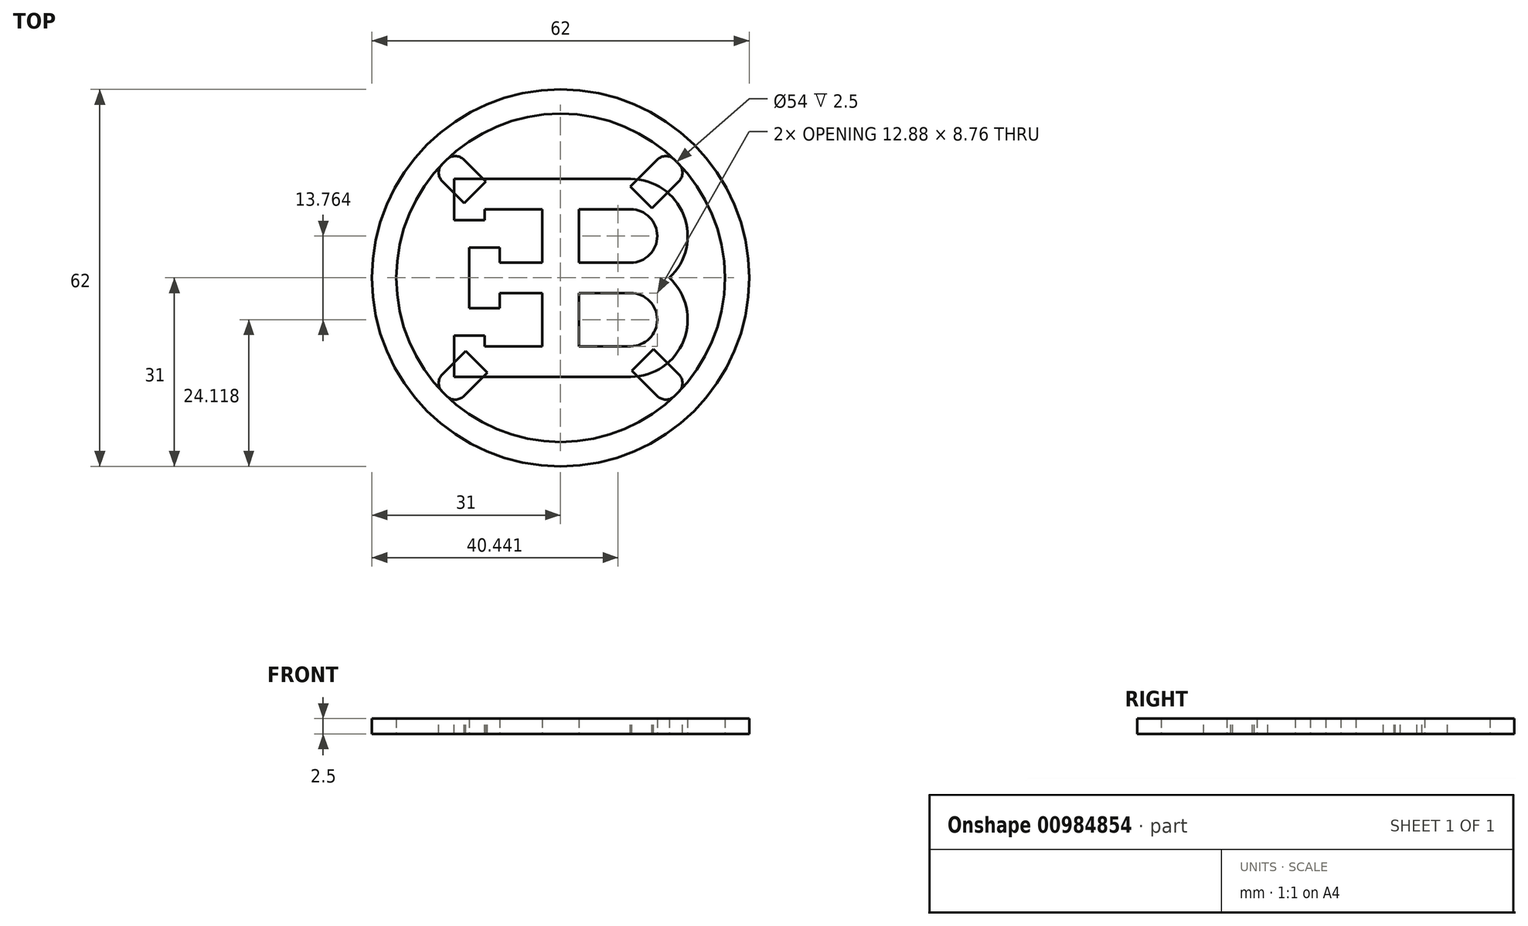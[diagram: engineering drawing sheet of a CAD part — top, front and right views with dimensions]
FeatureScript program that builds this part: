
annotation { "Feature Type Name" : "Feature", "Feature Type Description" : "" }
export const myFeature = defineFeature(function(context is Context, id is Id, definition is map)
    precondition{}
    {
        {
            var Q0;
            Q0=qCreatedBy(makeId("Front.planeOp"),FACE);
            var sketch = newSketch(context, id + "F0", { "sketchPlane" : qUnion([Q0])});
            skLineSegment(sketch, "E0.bottom", {"start": v(27, 0) * mm, "end": v(31, 0) * mm});
            skLineSegment(sketch, "E0.top", {"start": v(27, 2.5) * mm, "end": v(31, 2.5) * mm});
            skLineSegment(sketch, "E0.right", {"start": v(31, 0) * mm, "end": v(31, 2.5) * mm});
            skLineSegment(sketch, "E1", {"start": v(27, 2.5) * mm, "end": v(27, 0) * mm});
            skLineSegment(sketch, "E2", {"start": v(0, 0) * mm, "end": v(0, 16.47) * mm, "construction": true});
            skSolve(sketch);
        }
        {
            var Q0;
            Q0=qSketchRegion(id+"F0",true);
            var Q1;
            Q1=sQuery(id+"F0.wireOp",EDGE,"E2");
            revolve(context, id + "F1", {"surfaceOperationType" : NewSurfaceOperationType.NEW, "entities" : qUnion([Q0]), "axis" : qUnion([Q1]), "revolveType" : RevolveType.FULL});
        }
        {
            var Q0;
            Q0=qCreatedBy(makeId("Top.planeOp"),FACE);
            var sketch = newSketch(context, id + "F2", { "sketchPlane" : qUnion([Q0])});
            skLineSegment(sketch, "E3", {"start": v(0, 0) * mm, "end": v(-19.1, 19.1) * mm, "construction": true});
            skLineSegment(sketch, "E4", {"start": v(0, 0) * mm, "end": v(-19.1, -19.1) * mm, "construction": true});
            skLineSegment(sketch, "E5", {"start": v(0, 0) * mm, "end": v(-27, 0) * mm, "construction": true});
            skLineSegment(sketch, "E6", {"start": v(0, 0) * mm, "end": v(0, 27) * mm, "construction": true});
            skLineSegment(sketch, "E7", {"start": v(0, 0) * mm, "end": v(0, -27) * mm, "construction": true});
            skCircle(sketch, "E8", {"center": v(0, 0) * mm, "radius": 23 * mm, "construction": true});
            skLineSegment(sketch, "E9", {"start": v(-16.26, 16.26) * mm, "end": v(11.5, 16.26) * mm});
            skLineSegment(sketch, "E10", {"start": v(11.5, -16.26) * mm, "end": v(-16.26, -16.26) * mm});
            skLineSegment(sketch, "E11", {"start": v(-16.26, -16.26) * mm, "end": v(-16.26, -11.26) * mm});
            skLineSegment(sketch, "E12", {"start": v(-16.26, 11.26) * mm, "end": v(-3, 11.26) * mm});
            skLineSegment(sketch, "E13", {"start": v(-3, 11.26) * mm, "end": v(-3, 2.5) * mm});
            skLineSegment(sketch, "E14", {"start": v(-3, -11.26) * mm, "end": v(-16.26, -11.26) * mm});
            skLineSegment(sketch, "E15.trimOffspring", {"start": v(-16.26, 11.26) * mm, "end": v(-16.26, 16.26) * mm});
            skPoint(sketch, "E16.first.point", {"position": v(11.5, 16.26) * mm});
            skPoint(sketch, "E16.third.point", {"position": v(19.26, 12.58) * mm});
            skLineSegment(sketch, "E17", {"start": v(-3, 2.5) * mm, "end": v(-10, 2.5) * mm});
            skLineSegment(sketch, "E18", {"start": v(-10, -2.5) * mm, "end": v(-3, -2.5) * mm});
            skLineSegment(sketch, "E19.trimOffspring", {"start": v(-3, -2.5) * mm, "end": v(-3, -11.26) * mm});
            skLineSegment(sketch, "E20", {"start": v(-3, 2.5) * mm, "end": v(22.86, 2.5) * mm, "construction": true});
            skLineSegment(sketch, "E21", {"start": v(-3, -2.5) * mm, "end": v(22.86, -2.5) * mm, "construction": true});
            skLineSegment(sketch, "E22", {"start": v(3, 2.5) * mm, "end": v(3, 11.26) * mm});
            skLineSegment(sketch, "E23", {"start": v(3, 11.26) * mm, "end": v(11.5, 11.26) * mm});
            skLineSegment(sketch, "E24", {"start": v(3, 2.5) * mm, "end": v(11.5, 2.5) * mm});
            skArc(sketch, "E25", {"start": v(11.5, 11.26) * mm, "mid": v(15.88, 6.88) * mm, "end": v(11.5, 2.5) * mm});
            skArc(sketch, "E26.MirrorCS", {"start": v(11.5, -11.26) * mm, "mid": v(15.88, -6.88) * mm, "end": v(11.5, -2.5) * mm});
            skLineSegment(sketch, "E27.MirrorCS", {"start": v(3, -2.5) * mm, "end": v(3, -11.26) * mm});
            skLineSegment(sketch, "E28.MirrorCS", {"start": v(3, -11.26) * mm, "end": v(11.5, -11.26) * mm});
            skArc(sketch, "E29.trimOffspring", {"start": v(17.88, 0) * mm, "mid": v(20.23, -10.3) * mm, "end": v(11.5, -16.26) * mm});
            skArc(sketch, "E30.trimOffspring", {"start": v(17.88, 0) * mm, "mid": v(20.23, 10.3) * mm, "end": v(11.5, 16.26) * mm});
            skLineSegment(sketch, "E31", {"start": v(11.5, -2.5) * mm, "end": v(3, -2.5) * mm});
            skLineSegment(sketch, "E32.MirrorCS", {"start": v(0, 0) * mm, "end": v(19.1, 19.1) * mm, "construction": true});
            skLineSegment(sketch, "E33.MirrorCS", {"start": v(0, 0) * mm, "end": v(19.1, -19.1) * mm, "construction": true});
            skLineSegment(sketch, "E34.bottom", {"start": v(-15, -5) * mm, "end": v(-10, -5) * mm});
            skLineSegment(sketch, "E34.top", {"start": v(-15, 5) * mm, "end": v(-10, 5) * mm});
            skLineSegment(sketch, "E34.left", {"start": v(-15, -5) * mm, "end": v(-15, 5) * mm});
            skLineSegment(sketch, "E34.right", {"start": v(-10, -5) * mm, "end": v(-10, -2.5) * mm});
            skLineSegment(sketch, "E35.trimOffspring", {"start": v(-10, 2.5) * mm, "end": v(-10, 5) * mm});
            skSolve(sketch);
        }
        {
            var Q0;
            Q0=makeQuery(id+"F2.imprint","IMPRINT",FACE,{"disambiguationData":[TD([[makeQuery(id+"F2.imprint","IMPRINT",EDGE,{"derivedFrom":sQuery(id+"F2.wireOp",EDGE,"E9")}),-1.0]])]});
            var Q1;
            Q1=makeQuery(id+"F1.opRevolve","SWEPT_FACE",FACE,{"disambiguationData":[OSD([sQuery(id+"F0.wireOp",EDGE,"E0.top")])]});
            extrude(context, id + "F3", {"entities" : qUnion([Q0]), "endBound" : BoundingType.UP_TO_SURFACE, "depth" : 25 * mm, "endBoundEntityFace" : qUnion([Q1]), "offsetDistance" : 25 * mm});
        }
        {
            var Q0;
            Q0=makeQuery(id+"F3.opExtrude","CAP_FACE",FACE,{"disambiguationData":[OSD([sQuery(id+"F2.wireOp",EDGE,"E9"),sQuery(id+"F2.wireOp",EDGE,"E10"),sQuery(id+"F2.wireOp",EDGE,"E11"),sQuery(id+"F2.wireOp",EDGE,"E12"),sQuery(id+"F2.wireOp",EDGE,"E13"),sQuery(id+"F2.wireOp",EDGE,"E14"),sQuery(id+"F2.wireOp",EDGE,"E15.trimOffspring"),sQuery(id+"F2.wireOp",EDGE,"E17"),sQuery(id+"F2.wireOp",EDGE,"E18"),sQuery(id+"F2.wireOp",EDGE,"E19.trimOffspring"),sQuery(id+"F2.wireOp",EDGE,"E22"),sQuery(id+"F2.wireOp",EDGE,"E23"),sQuery(id+"F2.wireOp",EDGE,"E24"),sQuery(id+"F2.wireOp",EDGE,"E25"),sQuery(id+"F2.wireOp",EDGE,"E26.MirrorCS"),sQuery(id+"F2.wireOp",EDGE,"E27.MirrorCS"),sQuery(id+"F2.wireOp",EDGE,"E28.MirrorCS"),sQuery(id+"F2.wireOp",EDGE,"E29.trimOffspring"),sQuery(id+"F2.wireOp",EDGE,"E30.trimOffspring"),sQuery(id+"F2.wireOp",EDGE,"E31"),sQuery(id+"F2.wireOp",EDGE,"E34.bottom"),sQuery(id+"F2.wireOp",EDGE,"E34.top"),sQuery(id+"F2.wireOp",EDGE,"E34.left"),sQuery(id+"F2.wireOp",EDGE,"E34.right"),sQuery(id+"F2.wireOp",EDGE,"E35.trimOffspring")])],"isStart":false});
            var sketch = newSketch(context, id + "F4", { "sketchPlane" : qUnion([Q0])});
            skLineSegment(sketch, "E36", {"start": v(-12.5, 5) * mm, "end": v(-12.5, 16.26) * mm, "construction": true});
            skLineSegment(sketch, "E37", {"start": v(-12.5, -5) * mm, "end": v(-12.5, -16.26) * mm, "construction": true});
            skLineSegment(sketch, "E38.bottom", {"start": v(-12.5, 9.51) * mm, "end": v(-17.5, 9.51) * mm});
            skLineSegment(sketch, "E38.top", {"start": v(-12.5, 16.26) * mm, "end": v(-17.5, 16.26) * mm});
            skLineSegment(sketch, "E38.left", {"start": v(-12.5, 9.51) * mm, "end": v(-12.5, 16.26) * mm});
            skLineSegment(sketch, "E38.right", {"start": v(-17.5, 9.51) * mm, "end": v(-17.5, 16.26) * mm});
            skLineSegment(sketch, "E39.MirrorCS", {"start": v(-12.5, -9.51) * mm, "end": v(-17.5, -9.51) * mm});
            skLineSegment(sketch, "E40.MirrorCS", {"start": v(-12.5, -9.51) * mm, "end": v(-12.5, -16.26) * mm});
            skLineSegment(sketch, "E41.MirrorCS", {"start": v(-17.5, -9.51) * mm, "end": v(-17.5, -16.26) * mm});
            skLineSegment(sketch, "E42.MirrorCS", {"start": v(-12.5, -16.26) * mm, "end": v(-17.5, -16.26) * mm});
            skSolve(sketch);
        }
        {
            var Q0;
            {var subQ1=sQuery(id+"F4.wireOp",EDGE,"E38.bottom");Q0=makeQuery(id+"F4.imprint","IMPRINT",FACE,{"disambiguationData":[TD([[makeQuery(id+"F4.imprint","IMPRINT",EDGE,{"derivedFrom":subQ1}),-1.0]])]});}
            var Q1;
            {var subQ2=sQuery(id+"F4.wireOp",EDGE,"E39.MirrorCS");Q1=makeQuery(id+"F4.imprint","IMPRINT",FACE,{"disambiguationData":[TD([[makeQuery(id+"F4.imprint","IMPRINT",EDGE,{"derivedFrom":subQ2}),1.0]])]});}
            var Q2;
            Q2=makeQuery(id+"F3.opExtrude","CAP_FACE",FACE,{"disambiguationData":[OSD([sQuery(id+"F2.wireOp",EDGE,"E9"),sQuery(id+"F2.wireOp",EDGE,"E10"),sQuery(id+"F2.wireOp",EDGE,"E11"),sQuery(id+"F2.wireOp",EDGE,"E12"),sQuery(id+"F2.wireOp",EDGE,"E13"),sQuery(id+"F2.wireOp",EDGE,"E14"),sQuery(id+"F2.wireOp",EDGE,"E15.trimOffspring"),sQuery(id+"F2.wireOp",EDGE,"E17"),sQuery(id+"F2.wireOp",EDGE,"E18"),sQuery(id+"F2.wireOp",EDGE,"E19.trimOffspring"),sQuery(id+"F2.wireOp",EDGE,"E22"),sQuery(id+"F2.wireOp",EDGE,"E23"),sQuery(id+"F2.wireOp",EDGE,"E24"),sQuery(id+"F2.wireOp",EDGE,"E25"),sQuery(id+"F2.wireOp",EDGE,"E26.MirrorCS"),sQuery(id+"F2.wireOp",EDGE,"E27.MirrorCS"),sQuery(id+"F2.wireOp",EDGE,"E28.MirrorCS"),sQuery(id+"F2.wireOp",EDGE,"E29.trimOffspring"),sQuery(id+"F2.wireOp",EDGE,"E30.trimOffspring"),sQuery(id+"F2.wireOp",EDGE,"E31"),sQuery(id+"F2.wireOp",EDGE,"E34.bottom"),sQuery(id+"F2.wireOp",EDGE,"E34.top"),sQuery(id+"F2.wireOp",EDGE,"E34.left"),sQuery(id+"F2.wireOp",EDGE,"E34.right"),sQuery(id+"F2.wireOp",EDGE,"E35.trimOffspring")])],"isStart":true});
            extrude(context, id + "F5", {"entities" : qUnion([Q0, Q1]), "operationType" : NewBodyOperationType.ADD, "endBound" : BoundingType.UP_TO_SURFACE, "oppositeDirection" : true, "depth" : 25 * mm, "endBoundEntityFace" : qUnion([Q2]), "offsetDistance" : 25 * mm});
        }
        {
            var Q0;
            Q0=makeQuery(id+"F1.opRevolve","SWEPT_FACE",FACE,{"disambiguationData":[OSD([sQuery(id+"F0.wireOp",EDGE,"E0.top")])]});
            var sketch = newSketch(context, id + "F6", { "sketchPlane" : qUnion([Q0])});
            skLineSegment(sketch, "E43", {"start": v(0, 0) * mm, "end": v(-19.1, 19.1) * mm, "construction": true});
            skLineSegment(sketch, "E44", {"start": v(0, 0) * mm, "end": v(-19.1, -19.1) * mm, "construction": true});
            skLineSegment(sketch, "E45", {"start": v(0, 0) * mm, "end": v(19.1, 19.1) * mm, "construction": true});
            skLineSegment(sketch, "E46", {"start": v(0, 0) * mm, "end": v(19.1, -19.1) * mm, "construction": true});
            skLineSegment(sketch, "E47", {"start": v(-17.24, 20.78) * mm, "end": v(-12.28, 15.82) * mm});
            skLineSegment(sketch, "E48", {"start": v(-12.28, 15.82) * mm, "end": v(-15.82, 12.28) * mm});
            skLineSegment(sketch, "E49", {"start": v(-15.82, 12.28) * mm, "end": v(-20.78, 17.24) * mm});
            skLineSegment(sketch, "E50", {"start": v(17.24, -20.78) * mm, "end": v(11.74, -15.28) * mm});
            skLineSegment(sketch, "E51", {"start": v(11.74, -15.28) * mm, "end": v(15.28, -11.74) * mm});
            skLineSegment(sketch, "E52", {"start": v(15.28, -11.74) * mm, "end": v(20.78, -17.24) * mm});
            skLineSegment(sketch, "E53", {"start": v(-20.78, -17.24) * mm, "end": v(-15.6, -12.07) * mm});
            skLineSegment(sketch, "E54", {"start": v(-15.6, -12.07) * mm, "end": v(-12.06, -15.6) * mm});
            skLineSegment(sketch, "E55", {"start": v(-12.06, -15.6) * mm, "end": v(-17.24, -20.78) * mm});
            skLineSegment(sketch, "E56", {"start": v(17.24, 20.78) * mm, "end": v(11.47, 15) * mm});
            skLineSegment(sketch, "E57", {"start": v(11.47, 15) * mm, "end": v(15, 11.47) * mm});
            skLineSegment(sketch, "E58", {"start": v(15, 11.47) * mm, "end": v(20.78, 17.24) * mm});
            skSolve(sketch);
        }
        {
            var Q0;
            {var subQ0=sQuery(id+"F6.wireOp",EDGE,"E47");Q0=makeQuery(id+"F6.imprint","IMPRINT",FACE,{"disambiguationData":[TD([[makeQuery(id+"F6.imprint","IMPRINT",EDGE,{"derivedFrom":subQ0}),-1.0]])]});}
            var Q1;
            {var subQ0=sQuery(id+"F6.wireOp",EDGE,"E56");Q1=makeQuery(id+"F6.imprint","IMPRINT",FACE,{"disambiguationData":[TD([[makeQuery(id+"F6.imprint","IMPRINT",EDGE,{"derivedFrom":subQ0}),1.0]])]});}
            var Q2;
            {var subQ0=sQuery(id+"F6.wireOp",EDGE,"E50");Q2=makeQuery(id+"F6.imprint","IMPRINT",FACE,{"disambiguationData":[TD([[makeQuery(id+"F6.imprint","IMPRINT",EDGE,{"derivedFrom":subQ0}),-1.0]])]});}
            var Q3;
            {var subQ0=sQuery(id+"F6.wireOp",EDGE,"E53");Q3=makeQuery(id+"F6.imprint","IMPRINT",FACE,{"disambiguationData":[TD([[makeQuery(id+"F6.imprint","IMPRINT",EDGE,{"derivedFrom":subQ0}),-1.0]])]});}
            var Q4;
            Q4=makeQuery(id+"F1.opRevolve","SWEPT_FACE",FACE,{"disambiguationData":[OSD([sQuery(id+"F0.wireOp",EDGE,"E0.bottom")])]});
            extrude(context, id + "F7", {"entities" : qUnion([Q0, Q1, Q2, Q3]), "endBound" : BoundingType.UP_TO_SURFACE, "oppositeDirection" : true, "depth" : 25 * mm, "endBoundEntityFace" : qUnion([Q4]), "offsetDistance" : 25 * mm});
        }
        {
            var Q0;
            Q0=makeQuery(id+"F7.opExtrude","SWEPT_EDGE",EDGE,{"disambiguationData":[OSD([sQuery(id+"F0.wireOp",EDGE,"E0.top"),sQuery(id+"F0.wireOp",EDGE,"E1"),sQuery(id+"F6.wireOp",EDGE,"E47")])]});
            var Q1;
            Q1=makeQuery(id+"F7.opExtrude","SWEPT_EDGE",EDGE,{"disambiguationData":[OSD([sQuery(id+"F0.wireOp",EDGE,"E0.top"),sQuery(id+"F0.wireOp",EDGE,"E1"),sQuery(id+"F6.wireOp",EDGE,"E56")])]});
            fillet(context, id + "F8", {"entities" : qUnion([Q0, Q1]), "radius" : 2 * mm, "tangentPropagation" : true, "allowEdgeOverflow" : false});
        }
        {
            var Q0;
            Q0=makeQuery(id+"F7.opExtrude","SWEPT_EDGE",EDGE,{"disambiguationData":[OSD([sQuery(id+"F0.wireOp",EDGE,"E0.top"),sQuery(id+"F0.wireOp",EDGE,"E1"),sQuery(id+"F6.wireOp",EDGE,"E49")])]});
            var Q1;
            Q1=makeQuery(id+"F7.opExtrude","SWEPT_EDGE",EDGE,{"disambiguationData":[OSD([sQuery(id+"F0.wireOp",EDGE,"E0.top"),sQuery(id+"F0.wireOp",EDGE,"E1"),sQuery(id+"F6.wireOp",EDGE,"E53")])]});
            fillet(context, id + "F9", {"entities" : qUnion([Q0, Q1]), "radius" : 2 * mm, "tangentPropagation" : true, "allowEdgeOverflow" : false});
        }
        {
            var Q0;
            Q0=makeQuery(id+"F7.opExtrude","SWEPT_EDGE",EDGE,{"disambiguationData":[OSD([sQuery(id+"F0.wireOp",EDGE,"E0.top"),sQuery(id+"F0.wireOp",EDGE,"E1"),sQuery(id+"F6.wireOp",EDGE,"E55")])]});
            var Q1;
            Q1=makeQuery(id+"F7.opExtrude","SWEPT_EDGE",EDGE,{"disambiguationData":[OSD([sQuery(id+"F0.wireOp",EDGE,"E0.top"),sQuery(id+"F0.wireOp",EDGE,"E1"),sQuery(id+"F6.wireOp",EDGE,"E50")])]});
            fillet(context, id + "F10", {"entities" : qUnion([Q0, Q1]), "radius" : 2 * mm, "tangentPropagation" : true, "allowEdgeOverflow" : false});
        }
        {
            var Q0;
            Q0=makeQuery(id+"F7.opExtrude","SWEPT_EDGE",EDGE,{"disambiguationData":[OSD([sQuery(id+"F0.wireOp",EDGE,"E0.top"),sQuery(id+"F0.wireOp",EDGE,"E1"),sQuery(id+"F6.wireOp",EDGE,"E58")])]});
            var Q1;
            Q1=makeQuery(id+"F7.opExtrude","SWEPT_EDGE",EDGE,{"disambiguationData":[OSD([sQuery(id+"F0.wireOp",EDGE,"E0.top"),sQuery(id+"F0.wireOp",EDGE,"E1"),sQuery(id+"F6.wireOp",EDGE,"E52")])]});
            fillet(context, id + "F11", {"entities" : qUnion([Q0, Q1]), "radius" : 2 * mm, "tangentPropagation" : true, "allowEdgeOverflow" : false});
        }
    });
